SOLIDWORKS PART (.sldprt)
format: sldprt  version: not decoded by parser v0  size: 223,232 bytes
history: native  units: mm
features: fillet x6, sketch x2, material x1, extrude x1, cut_extrude x1 (+11 scaffold rows collapsed)
feature tree (22):
  scaffold x11  (default folders/planes/origin — collapsed)
  material  "Material <not specified>"
  sketch  "Sketch1"  dims[D1=0.5mm D2=1.5mm]
  extrude  "Boss-Extrude1"  [1 undecoded]
  fillet  "Fillet1"  Radius=10mm
  fillet  "Fillet2"  Radius=10mm
  fillet  "Fillet3"  Radius=0.5mm
  fillet  "Fillet4"  Radius=0.5mm
  sketch  "Sketch2"  dims[D1=2.0mm D2=2.0mm D3=3.0]
  cut_extrude  "Cut-Extrude1"  Depth=40mm
  fillet  "Fillet5"  Radius=0.25mm
  fillet  "Fillet6"  Radius=0.25mm
decode coverage: 9 of 10 modeling features carry decoded parameters
note: 1 parameter value undecoded
note: suppression state not decoded; provenance and decode notes live in map.json
